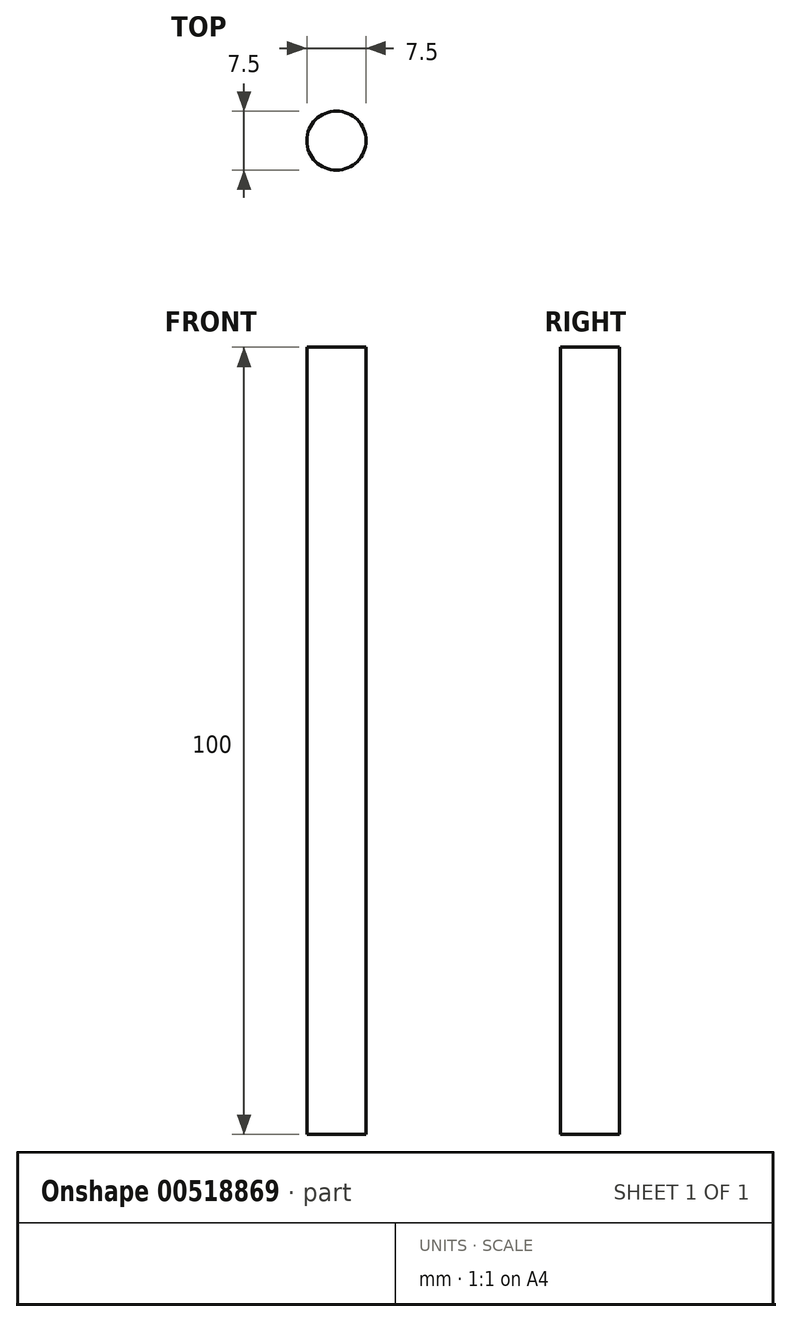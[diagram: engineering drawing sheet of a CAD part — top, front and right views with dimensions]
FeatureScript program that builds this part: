
annotation { "Feature Type Name" : "Feature", "Feature Type Description" : "" }
export const myFeature = defineFeature(function(context is Context, id is Id, definition is map)
    precondition{}
    {
        {
            var Q0;
            Q0=qCreatedBy(makeId("Top.planeOp"),FACE);
            var sketch = newSketch(context, id + "F0", { "sketchPlane" : qUnion([Q0])});
            skCircle(sketch, "E0", {"center": v(0, 0) * mm, "radius": 3.75 * mm});
            skSolve(sketch);
        }
        {
            var Q0;
            Q0=sQuery(id+"F0.wireOp",EDGE,"E0");
            extrude(context, id + "F1", {"bodyType" : ToolBodyType.SURFACE, "surfaceEntities" : qUnion([Q0]), "depth" : 100 * mm, "offsetDistance" : 25 * mm});
        }
    });
